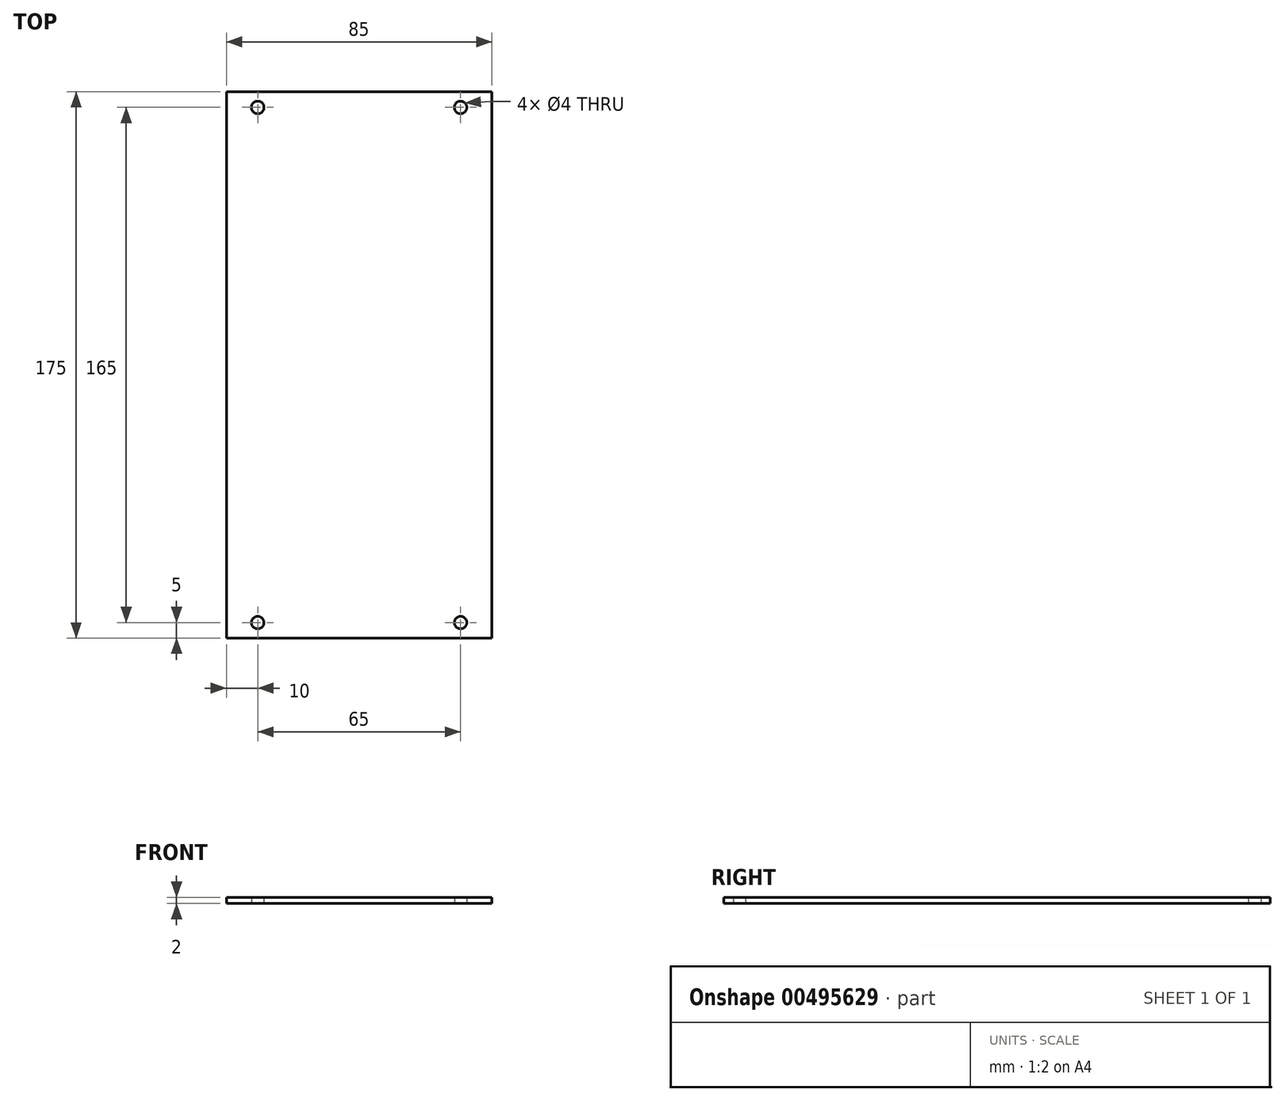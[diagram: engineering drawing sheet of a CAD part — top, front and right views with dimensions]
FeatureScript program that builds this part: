
annotation { "Feature Type Name" : "Feature", "Feature Type Description" : "" }
export const myFeature = defineFeature(function(context is Context, id is Id, definition is map)
    precondition{}
    {
        {
            var Q0;
            Q0=qCreatedBy(makeId("Top.planeOp"),FACE);
            var sketch = newSketch(context, id + "F0", { "sketchPlane" : qUnion([Q0])});
            skLineSegment(sketch, "E0.bottom", {"start": v(0, 0) * mm, "end": v(85, 0) * mm});
            skLineSegment(sketch, "E0.top", {"start": v(0, 175) * mm, "end": v(85, 175) * mm});
            skLineSegment(sketch, "E0.left", {"start": v(0, 0) * mm, "end": v(0, 175) * mm});
            skLineSegment(sketch, "E0.right", {"start": v(85, 0) * mm, "end": v(85, 175) * mm});
            skCircle(sketch, "E1", {"center": v(10, 5) * mm, "radius": 2 * mm});
            skCircle(sketch, "E2", {"center": v(75, 5) * mm, "radius": 2 * mm});
            skCircle(sketch, "E3", {"center": v(10, 170) * mm, "radius": 2 * mm});
            skCircle(sketch, "E4", {"center": v(75, 170) * mm, "radius": 2 * mm});
            skSolve(sketch);
        }
        {
            var Q0;
            Q0=makeQuery(id+"F0.imprint","IMPRINT",FACE,{"disambiguationData":[TD([[makeQuery(id+"F0.imprint","IMPRINT",EDGE,{"derivedFrom":sQuery(id+"F0.wireOp",EDGE,"E0.bottom")}),1.0]])]});
            extrude(context, id + "F1", {"entities" : qUnion([Q0]), "depth" : 2 * mm});
        }
    });
